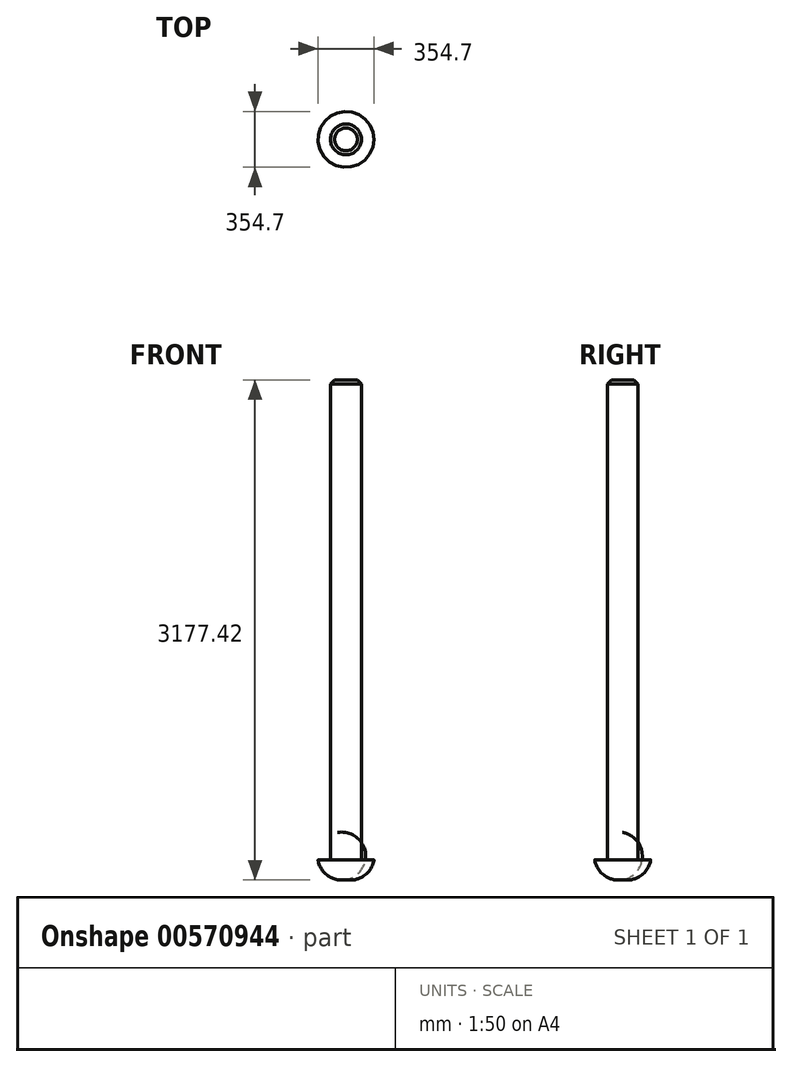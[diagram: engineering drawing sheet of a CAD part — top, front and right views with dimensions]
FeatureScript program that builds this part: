
annotation { "Feature Type Name" : "Feature", "Feature Type Description" : "" }
export const myFeature = defineFeature(function(context is Context, id is Id, definition is map)
    precondition{}
    {
        {
            var Q0;
            Q0=qCreatedBy(makeId("Top.planeOp"),FACE);
            var sketch = newSketch(context, id + "F0", { "sketchPlane" : qUnion([Q0])});
            skCircle(sketch, "E0", {"center": v(0, 0) * mm, "radius": 97.8 * mm});
            skSolve(sketch);
        }
        {
            var Q0;
            Q0 = qSketchRegion(id + "F0", true);
            extrude(context, id + "F1", {"entities" : qUnion([Q0]), "depth" : 3048 * mm, "offsetDistance" : 25.4 * mm});
        }
        {
            var Q0;
            Q0=qCreatedBy(makeId("Front.planeOp"),FACE);
            var sketch = newSketch(context, id + "F2", { "sketchPlane" : qUnion([Q0])});
            skLineSegment(sketch, "E1", {"start": v(177.8, 0) * mm, "end": v(177.8, 0) * mm});
            skLineSegment(sketch, "E2", {"start": v(0, 0) * mm, "end": v(0, -127) * mm});
            skArc(sketch, "E3", {"start": v(0, -127) * mm, "mid": v(115.7, -101.02) * mm, "end": v(177.8, 0) * mm});
            skLineSegment(sketch, "E4", {"start": v(177.8, 0) * mm, "end": v(0, 0) * mm});
            skSolve(sketch);
        }
        {
            var Q0;
            Q0=makeQuery(id+"F2.imprint","IMPRINT",FACE,{"disambiguationData":[TD([[makeQuery(id+"F2.imprint","IMPRINT",EDGE,{"derivedFrom":sQuery(id+"F2.wireOp",EDGE,"E2")}),1.0]])]});
            var Q1;
            Q1=makeQuery(id+"F1.opExtrude","CAP_EDGE",EDGE,{"disambiguationData":[OSD([sQuery(id+"F0.wireOp",EDGE,"E0")])],"isStart":true});
            revolve(context, id + "F3", {"operationType" : NewBodyOperationType.ADD, "entities" : qUnion([Q0]), "axis" : qUnion([Q1]), "revolveType" : RevolveType.FULL});
        }
        {
            var Q0;
            Q0=makeQuery(id+"F3.opRevolve","SWEPT_EDGE",EDGE,{"disambiguationData":[OSD([sQuery(id+"F2.wireOp",EDGE,"E3"),sQuery(id+"F2.wireOp",EDGE,"E4")])]});
            fillet(context, id + "F4", {"entities" : qUnion([Q0]), "radius" : 2.54 * mm, "tangentPropagation" : true, "allowEdgeOverflow" : false});
        }
        {
            var Q0;
            Q0=makeQuery(id+"F1.opExtrude","CAP_EDGE",EDGE,{"disambiguationData":[OSD([sQuery(id+"F0.wireOp",EDGE,"E0")])],"isStart":false});
            chamfer(context, id + "F5", {"entities" : qUnion([Q0]), "width" : 25.4 * mm, "tangentPropagation" : true});
        }
    });
